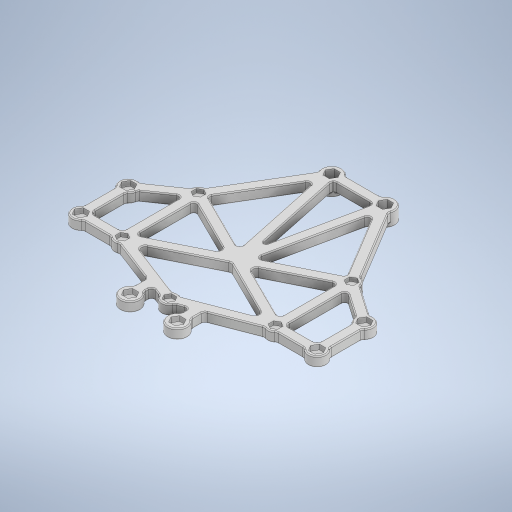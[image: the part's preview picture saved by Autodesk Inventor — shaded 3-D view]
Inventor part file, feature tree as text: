
AUTODESK INVENTOR PART (.ipt)
format: ipt  version: 2024.2 (Build 282272000, 272)  size: 1,575,424 bytes
history: native  units: mm
features: projected_geometry x67, extrude x8, sketch x6, fillet x5, hole x2
ambient origin geometry x8: Origin, YZ Plane, XZ Plane, XY Plane, X Axis, Y Axis, Z Axis, Center Point
bodies: Solid1 (feature_tree)
feature tree (88):
  sketch  "Sketch1"  dims[d0=4.8mm d9=5.6mm]
  extrude  "Extrusion1"  Depth=5.6mm
  sketch  "Sketch2"  dims[d10=24.0mm d11=9.0mm]
  extrude  "Extrusion2"  Depth=9.0mm
  extrude  "Extrusion3"  Depth=5.0mm
  extrude  "Extrusion4"  Depth=2.5mm
  extrude  "Extrusion5"  Depth=2.5mm
  hole  "Hole1"  [1 undecoded]
  hole  "Hole2"  [1 undecoded]
  fillet  "Fillet1"  Radius=2.5mm
  fillet  "Fillet2"  Radius=2.5mm
  fillet  "Fillet3"  Radius=5.0mm
  fillet  "Fillet7"  Radius=2.5mm
  fillet  "Fillet8"  Radius=5.0mm
  extrude  "Extrusion6"  Depth=2.5mm
  extrude  "Extrusion7"  Depth=2.5mm
  extrude  "Extrusion8"  Depth=2.5mm
  projected_geometry  "Projected Loop1"
  projected_geometry  "Projected Loop2"
  projected_geometry  "Projected Loop3"
  projected_geometry  "Projected Loop4"
  projected_geometry  "Projected Loop5"
  projected_geometry  "Projected Loop6"
  projected_geometry  "Projected Loop7"
  projected_geometry  "Projected Loop8"
  projected_geometry  "Projected Loop9"
  projected_geometry  "Projected Loop10"
  projected_geometry  "Projected Loop11"
  projected_geometry  "Projected Loop12"
  projected_geometry  "Projected Loop13"
  projected_geometry  "Projected Loop14"
  projected_geometry  "Projected Loop15"
  projected_geometry  "Projected Loop16"
  projected_geometry  "Projected Loop17"
  projected_geometry  "Projected Loop18"
  projected_geometry  "Projected Loop19"
  projected_geometry  "Projected Loop20"
  projected_geometry  "Projected Loop21"
  projected_geometry  "Projected Loop22"
  projected_geometry  "Projected Loop23"
  projected_geometry  "Projected Loop24"
  projected_geometry  "Projected Loop25"
  projected_geometry  "Projected Loop26"
  projected_geometry  "Projected Loop27"
  projected_geometry  "Projected Loop28"
  projected_geometry  "Projected Loop29"
  projected_geometry  "Projected Loop30"
  projected_geometry  "Projected Loop31"
  projected_geometry  "Projected Loop32"
  projected_geometry  "Projected Loop33"
  projected_geometry  "Projected Loop34"
  projected_geometry  "Projected Loop35"
  projected_geometry  "Projected Loop36"
  projected_geometry  "Projected Loop37"
  projected_geometry  "Projected Loop38"
  projected_geometry  "Projected Loop39"
  projected_geometry  "Projected Loop40"
  projected_geometry  "Projected Loop41"
  projected_geometry  "Projected Loop42"
  projected_geometry  "Projected Loop43"
  projected_geometry  "Projected Loop44"
  projected_geometry  "Projected Loop45"
  projected_geometry  "Projected Loop46"
  projected_geometry  "Projected Loop47"
  projected_geometry  "Projected Loop48"
  projected_geometry  "Projected Loop49"
  projected_geometry  "Projected Loop50"
  projected_geometry  "Projected Loop51"
  projected_geometry  "Projected Loop52"
  projected_geometry  "Projected Loop53"
  projected_geometry  "Projected Loop54"
  projected_geometry  "Projected Loop55"
  projected_geometry  "Projected Loop56"
  projected_geometry  "Projected Loop57"
  projected_geometry  "Projected Loop58"
  projected_geometry  "Projected Loop59"
  projected_geometry  "Projected Loop60"
  projected_geometry  "Projected Loop61"
  projected_geometry  "Projected Loop62"
  projected_geometry  "Projected Loop63"
  projected_geometry  "Projected Loop64"
  projected_geometry  "Projected Loop65"
  projected_geometry  "Projected Loop66"
  projected_geometry  "Projected Loop67"
  sketch  "Sketch3"  dims[d16=120.0mm d17=5.0mm]
  sketch  "Sketch4"  dims[d18=2.5mm d22=5.0mm]
  sketch  "Sketch6"  dims[d23=2.5mm d24=2.5mm]
  sketch  "Sketch7"  dims[d25=2.5mm d26=2.5mm d27=5.0mm d28=2.5mm d29=2.5mm d30=5.0mm d31=2.5mm d32=5.0mm d33=2.5mm d34=2.5mm d35=2.5mm d36=5.0mm d37=2.5mm d42=27.0mm d48=2.5mm d51=12.0mm d52=8.0mm d53=10.0mm d55=8.0mm d56=5.0mm d57=2.5mm d58=24.0mm d59=5.0mm d60=0.0mm d61=1.9mm d62=0.0mm d63=2.5mm d64=0.0mm d65=3.5mm d66=6.0mm d67=4.0mm d68=2.0mm d69=90.0deg d70=6.0mm d71=0.0mm d72=5.25mm d73=6.0mm d74=4.0mm d75=2.0mm d76=90.0deg d77=1.0mm d78=0.0mm d79=5.0mm d80=0.0mm d81=2.0mm d82=2.0mm d83=1.5mm d90=96.0mm d91=5.0mm d92=2.5mm d95=2.5mm d96=2.5mm d97=2.5mm d98=5.0mm d100=2.0mm d101=0.0mm d102=5.0mm d103=15.0mm d104=2.5mm d105=2.5mm d106=2.5mm d107=5.0mm d108=5.0mm d109=2.5mm d110=42.0mm d127=73.0mm d128=60.0mm d129=0.2mm d130=0.0mm d131=0.2mm d132=0.0mm d133=0.2mm d134=0.0mm d135=5.0mm d136=2.5mm d137=5.0mm d138=2.5mm d139=8.0mm d140=1.0mm d141=0.5mm d84=0.0mm d85=0.0mm d86=0.0mm d87=0.0mm]
note: 2 required parameter values undecoded (feature->parameter linkage not recoverable at this tier; creation-order binding heuristic only, values carry confidence <= 0.55)
